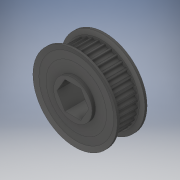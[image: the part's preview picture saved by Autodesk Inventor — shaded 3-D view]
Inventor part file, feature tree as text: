
AUTODESK INVENTOR PART (.ipt)
format: ipt  version: 2018 (Build 220112000, 112)  size: 401,920 bytes
history: native  units: in
note: dims shown in document units (in); Inventor stores cm internally (conversion verified against a paired STEP export)
features: revolve x2, other x1
ambient origin geometry x8: Origin, YZ Plane, XZ Plane, XY Plane, X Axis, Y Axis, Z Axis, Center Point
bodies: Solid1 (feature_tree), Solid2 (feature_tree), Solid3 (feature_tree)
feature tree (3):
  revolve  "Revolve1[1]"  [1 undecoded]
  revolve  "Revolve1[2]"  [1 undecoded]
  other  "Cut-Extrude4"
note: 2 required parameter values undecoded (feature->parameter linkage not recoverable at this tier; creation-order binding heuristic only, values carry confidence <= 0.55)
